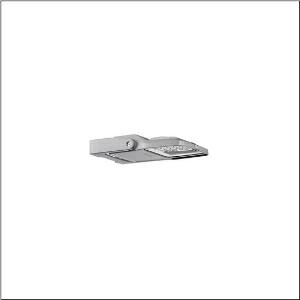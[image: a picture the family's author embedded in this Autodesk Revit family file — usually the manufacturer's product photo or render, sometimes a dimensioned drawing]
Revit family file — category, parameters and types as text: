
# Revit family: floodlight_fl_21_iq_micro___pl33t_5xa7762a2f2a_46b5
name_source: partatom
category: Lighting Fixtures
units: mm (PartAtom-declared; Revit-internal decimal feet)

## family parameters
Cut with Voids When Loaded = No
Host = Face
Light Source = No
Part Type = Normal
Room Calculation Point = No
Round Connector Dimension = Use Diameter
Shared = No

## types (1)
- --- (1 x LED, 2930 lm, 23.1 W, 3000K)
    Apparent Load = 23 VA
    CIE Flux Codes = 26 75 99 100 100
    Color Rendering = 70
    Color Temperature = 3000K
    Default Elevation = 1800 mm
    Description = Floodlight FL 21 iQ micro, floodlight, primary light control with lens, of PMMA, primary optical cover: protective disc, of toughened safety glass, transparent, light distribution: PL33T, light emission: direct distribution, installation type: surface-mounted, LED, High Power LED, rated luminous flux: 2.930lm, luminous efficacy: 127lm/W, light colour: 730, colour temperature: 3000K, control: Auto-Match, Temp-Guard, Night-Set, Smart-Wire, Desk-Remote (wireless, voltage-free reading and setting of iQ features in the workshop via application-optimized NFC function/RFID function), optimised constant luminous flux control (CLO 2.0), Street-Remote, with terminal, 6-pole, mains connection: 220..240V, AC, 50/60Hz, start of lifetime: 23W, end of service life: 24W, reduction: 11W, luminaire housing, of diecast aluminium, powder-coated, Siteco® metallic grey (DB 702S), corrosivity category C5 mid according to DIN EN ISO 12944, sealing non-destructively replaceable, design bracket, of diecast aluminium, powder-coated, Siteco® metallic grey (DB 702S), protection rating (complete): IP66, insulation class (complete): insulation class II (safety insulation), certification: CE, ENEC, VDE, protection symbol: D, impact resistance: IK07, permissible operating ambient temperature: -40..+40°C, permissible operating ambient temperature for outdoor applications: -40..+50°C, standard: DIN EN 12944, LABS conformity tested according to VDMA 24364:2018-05, packaging unit: 1 piece

Light Distribution: PL33T
    Height = 65 mm
    Lamp = 1 x LED
    Lamp Light Flux = 2930 lm
    Lamp Power = 23.1 W
    Lamp count = 1
    Length = 312 mm
    Luminous efficacy = 127 lm/W
    Manufacturer = Siteco
    ModVariant = No
    Model = 5XA7762A2F2A
    Mounting Place = Wall
    Mounting Type = Surface mounted
    Number of Poles = 1
    OnlyDefault = Yes
    Power Factor = 1
    Product Name = Floodlight FL 21 iQ micro | PL33T
    Product group = floodlight | wall mounted
    ProductGroupID = 2001
    Protection Class = Protection class II
    Protection Degree = IP 66
    RLX_Detail_Level = 1
    RLX_Emergency_Light_Flux = 0 lm
    RLX_Emergency_Type = 0
    RLX_Emergency_Type_DB = No
    RlxData = <blob elided: 97165 chars, md5=ec36353d>
    Socket = socket
    Standby Power = 0 W
    System Light Flux = 2930 lm
    System Power = 23 W
    Type Comments = factory setting: luminous flux: 100 % | dim-lin: 254 | 455 mA
    Type Image = l_1006878.jpg
    URL = http://relux.com
    VarID = @adj_098167
    Voltage = 0 V
    Weight = 0.00 kg
    Width = 230 mm

## geometry (parser evidence)
native form markers: Blend x4, Sweep x13
no freeform markers — native parametric forms only
